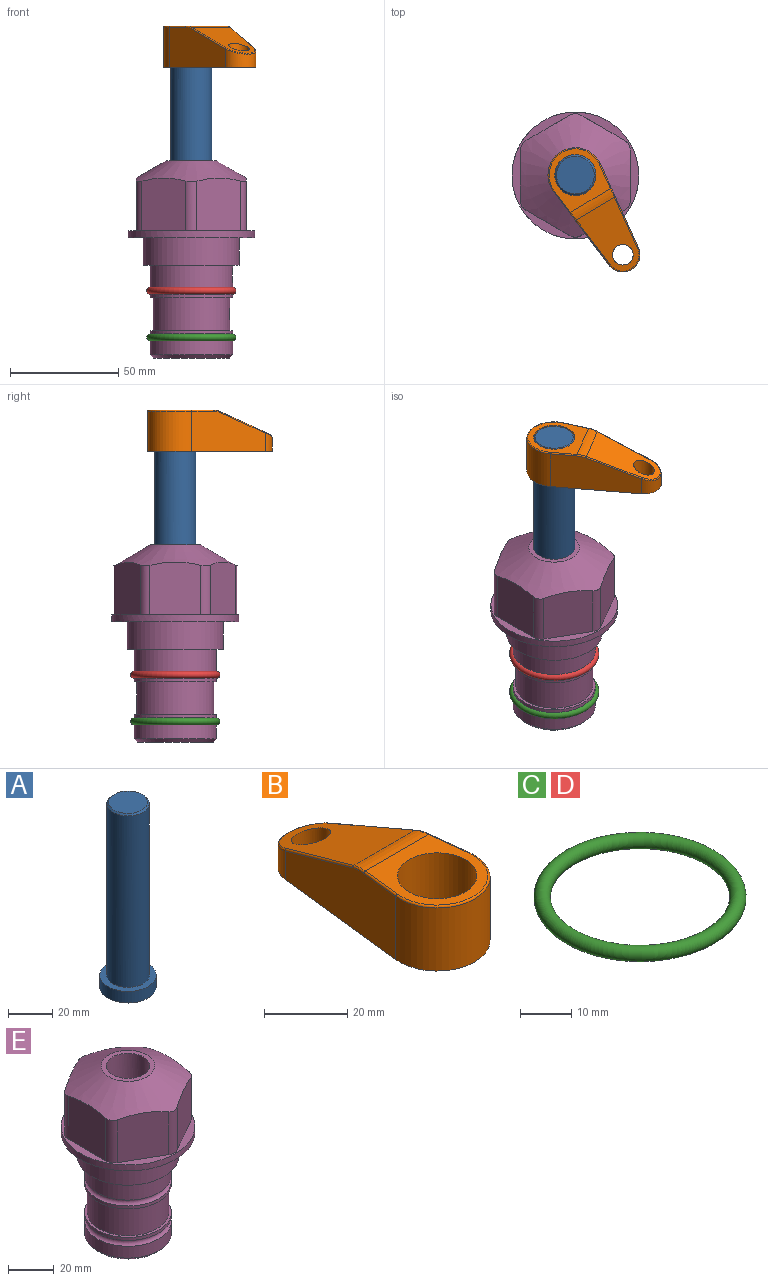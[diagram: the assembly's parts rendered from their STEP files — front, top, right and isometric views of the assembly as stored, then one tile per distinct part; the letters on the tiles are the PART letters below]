
ASSEMBLY  parts=5 mates=3
PART A: 6 faces, bbox 25.4x25.4x101.6 mm
  f0: plane 17.46x17.46mm, normal (0,0,1), area 239.5mm2, adj f5
  f1: plane 25.4x25.4mm, normal (0,0,-1), area 506.7mm2, adj f2
  f2: cylinder r=12.7mm len=25.4mm, axis (0,0,1), area 506.7mm2, adj f1,f3
  f3: plane 25.4x25.4mm, normal (0,0,1), area 221.7mm2, adj f2,f4
  f4: cylinder r=9.53mm len=94.46mm, axis (0,0,1), area 5653mm2, adj f3,f5
  f5: cone r=8.73mm half-angle=45deg, axis (0,0,-1), area 64.4mm2, adj f0,f4
PART B: 44 faces, bbox 27.5x64.5x19.1 mm
  f0: plane 2.3x0.95mm, normal (0,0,-1), area 1mm2, adj f25,f30,f34
  f1: plane 63.5x25.4mm, normal (0,0,-1), area 561.7mm2, adj f2,f3,f4,f5,f6,f7,f19,f20
  f2: cylinder r=12.7mm len=25.4mm, axis (0,0,-1), area 792.2mm2, adj f1,f3,f5,f13
  f3: plane 42.33x18.54mm, normal (0.99,0.11,0), area 647mm2, adj f1,f2,f4,f11,f12,f14
  f4: cylinder r=7.94mm len=15.78mm, axis (0,0,-1), area 158.6mm2, adj f1,f3,f5,f16
  f5: plane 42.33x18.54mm, normal (-0.99,0.11,0), area 647mm2, adj f1,f2,f4,f15,f17,f18
  f6: cylinder r=9.53mm len=19.05mm, axis (0,0,-1), area 1140.1mm2, adj f1,f8
  f7: cylinder r=4.76mm len=10.98mm, axis (0,0,-1), area 276.1mm2, adj f1,f9
  f8: plane 25.83x24.38mm, normal (0,0,1), area 262.2mm2, adj f6,f10,f11,f13,f15
  f9: plane 32.49x20.55mm, normal (0,0.34,0.94), area 489.9mm2, adj f7,f10,f14,f16,f18
  f10: cylinder r=12.7mm len=21.49mm, axis (-1,0,0), area 93.2mm2, adj f8,f9,f12,f17
  f11: cylinder r=0.51mm len=12.34mm, axis (0.11,-0.99,0), area 9.9mm2, adj f3,f8,f12,f13
  f12: bspline ~7.62x1.64mm, area 3.5mm2, adj f3,f10,f11,f14
  f13: torus R=12.19mm, axis (0,0,1), area 33.6mm2, adj f2,f8,f11,f15
  f14: cylinder r=0.51mm len=26.01mm, axis (0.1,-0.93,0.34), area 21.6mm2, adj f3,f9,f12,f16
  f15: cylinder r=0.51mm len=12.34mm, axis (0.11,0.99,0), area 9.9mm2, adj f5,f8,f13,f17
  f16: bspline ~15.78x7.05mm, area 15.7mm2, adj f4,f9,f14,f18
  f17: bspline ~7.62x1.64mm, area 3.5mm2, adj f5,f10,f15,f18
  f18: cylinder r=0.51mm len=26.01mm, axis (0.1,0.93,-0.34), area 21.6mm2, adj f5,f9,f16,f17
  f19: plane 21.6x14.29mm, normal (-0.99,-0.11,0), area 242.6mm2, adj f1,f26,f28,f34,f36,f38
  f20: plane 21.6x14.29mm, normal (0.99,-0.11,0), area 242.6mm2, adj f1,f27,f29,f37,f39,f41
  f21: cylinder r=12.7mm len=14.29mm, axis (0,0,-1), area 173.2mm2, adj f1,f26,f27,f30,f31,f33
  f22: cylinder r=7.94mm len=7.63mm, axis (0,0,-1), area 53.8mm2, adj f1,f28,f29,f42
  f23: plane 2.3x0.95mm, normal (0,0,-1), area 1mm2, adj f25,f33,f37
  f24: plane 17.94x12.32mm, normal (0,-0.34,-0.94), area 191.2mm2, adj f25,f38,f41,f42
  f25: cylinder r=9.53mm len=12.93mm, axis (-1,0,0), area 37.5mm2, adj f0,f23,f24,f31,f36,f39
  f26: cylinder r=1.59mm len=14.29mm, axis (0,0,-1), area 49mm2, adj f1,f19,f21,f32
  f27: cylinder r=1.59mm len=14.29mm, axis (0,0,-1), area 49mm2, adj f1,f20,f21,f35
  f28: cylinder r=1.59mm len=7.28mm, axis (0,0,-1), area 22.1mm2, adj f1,f19,f22,f40
  f29: cylinder r=1.59mm len=7.28mm, axis (0,0,-1), area 22.1mm2, adj f1,f20,f22,f43
  f30: torus R=14.29mm, axis (0,0,1), area 5.8mm2, adj f0,f21,f31,f32
  f31: bspline ~11.06x2.73mm, area 20.8mm2, adj f21,f25,f30,f33
  f32: sphere r=1.59mm, area 5.4mm2, adj f26,f30,f34
  f33: torus R=14.29mm, axis (0,0,1), area 5.8mm2, adj f21,f23,f31,f35
  f34: cylinder r=1.59mm len=1.68mm, axis (-0.11,0.99,0), area 2.4mm2, adj f0,f19,f32,f36
  f35: sphere r=1.59mm, area 5.4mm2, adj f27,f33,f37
  f36: bspline ~5.82x2.33mm, area 7.7mm2, adj f19,f25,f34,f38
  f37: cylinder r=1.59mm len=1.68mm, axis (0.11,0.99,0), area 2.4mm2, adj f20,f23,f35,f39
  f38: cylinder r=1.59mm len=18.33mm, axis (0.1,-0.93,0.34), area 46.7mm2, adj f19,f24,f36,f40
  f39: bspline ~5.82x2.33mm, area 7.7mm2, adj f20,f25,f37,f41
  f40: sphere r=1.59mm, area 3.6mm2, adj f28,f38,f42
  f41: cylinder r=1.59mm len=18.33mm, axis (0.1,0.93,-0.34), area 46.7mm2, adj f20,f24,f39,f43
  f42: bspline ~8.31x1.84mm, area 15.3mm2, adj f22,f24,f40,f43
  f43: sphere r=1.59mm, area 3.6mm2, adj f29,f41,f42
PART C: 1 faces, bbox 44.7x44.7x3.2 mm
  f0: torus R=19.05mm, axis (0,0,1), area 1193.9mm2
PART D: same geometry as C
PART E: 36 faces, bbox 58.7x58.7x91.2 mm
  f0: cylinder r=17.78mm len=35.56mm, axis (0,0,1), area 1670.8mm2, adj f23,f24,f31
  f1: cylinder r=19.05mm len=38.1mm, axis (0,0,1), area 1191.9mm2, adj f26,f27,f30
  f2: plane 58.66x58.66mm, normal (0,0,-1), area 1150.6mm2, adj f3,f28
  f3: cylinder r=29.33mm len=58.66mm, axis (0,0,-1), area 585.1mm2, adj f2,f4
  f4: plane 58.66x58.66mm, normal (0,0,1), area 475.9mm2, adj f3,f5,f6,f7,f8,f9,f10,f11
  f5: plane 24.5x20.32mm, normal (-0.5,0.87,0), area 562.8mm2, adj f4,f15,f16,f17
  f6: plane 24.5x20.32mm, normal (0.5,0.87,0), area 562.8mm2, adj f4,f14,f15,f17
  f7: plane 24.5x23.48mm, normal (1,0,0), area 562.8mm2, adj f4,f13,f14,f17
  f8: plane 24.5x20.32mm, normal (0.5,-0.87,0), area 562.8mm2, adj f4,f12,f13,f17
  f9: plane 24.5x20.32mm, normal (-0.5,-0.87,0), area 562.8mm2, adj f4,f11,f12,f17
  f10: plane 24.5x23.48mm, normal (-1,0,0), area 562.8mm2, adj f4,f11,f16,f17
  f11: cylinder r=5.08mm len=23.01mm, axis (0,0,-1), area 121.2mm2, adj f4,f9,f10,f17
  f12: cylinder r=5.08mm len=23.01mm, axis (0,0,-1), area 121.2mm2, adj f4,f8,f9,f17
  f13: cylinder r=5.08mm len=23.01mm, axis (0,0,-1), area 121.2mm2, adj f4,f7,f8,f17
  f14: cylinder r=5.08mm len=23.01mm, axis (0,0,-1), area 121.2mm2, adj f4,f6,f7,f17
  f15: cylinder r=5.08mm len=23.01mm, axis (0,0,-1), area 121.2mm2, adj f4,f5,f6,f17
  f16: cylinder r=5.08mm len=23.01mm, axis (0,0,-1), area 121.2mm2, adj f4,f5,f10,f17
  f17: cone r=11.73mm half-angle=60deg, axis (0,0,-1), area 2071.8mm2, adj f5,f6,f7,f8,f9,f10,f11,f12
  f18: plane 23.46x23.46mm, normal (0,0,1), area 147.4mm2, adj f17,f35
  f19: plane 34.93x34.93mm, normal (0,0,-1), area 958mm2, adj f29
  f20: cylinder r=19.05mm len=38.1mm, axis (0,0,1), area 760.1mm2, adj f21,f29
  f21: torus R=19.05mm, axis (0,0,1), area 565.3mm2, adj f20,f22
  f22: cylinder r=19.05mm len=38.1mm, axis (0,0,1), area 190mm2, adj f21,f23
  f23: plane 38.1x38.1mm, normal (0,0,1), area 146.9mm2, adj f0,f22
  f24: plane 38.1x38.1mm, normal (0,0,-1), area 146.9mm2, adj f0,f25
  f25: cylinder r=19.05mm len=38.1mm, axis (0,0,1), area 190mm2, adj f24,f26
  f26: torus R=19.05mm, axis (0,0,1), area 565.3mm2, adj f1,f25
  f27: plane 44.45x44.45mm, normal (0,0,-1), area 411.7mm2, adj f1,f28
  f28: cylinder r=22.23mm len=44.45mm, axis (0,0,1), area 1773.5mm2, adj f2,f27
  f29: cone r=19.05mm half-angle=45deg, axis (0,0,1), area 257.5mm2, adj f19,f20
  f30: cylinder r=3.17mm len=6.75mm, axis (-1,0,0), area 128mm2, adj f1,f33
  f31: cylinder r=3.17mm len=6.35mm, axis (-1,0,0), area 102.5mm2, adj f0,f33
  f32: plane 25.4x25.4mm, normal (0,0,1), area 506.7mm2, adj f33
  f33: cylinder r=12.7mm len=66.42mm, axis (0,0,-1), area 5236.2mm2, adj f30,f31,f32,f34
  f34: cone r=9.53mm half-angle=30deg, axis (0,0,-1), area 443.4mm2, adj f33,f35
  f35: cylinder r=9.53mm len=19.05mm, axis (0,0,-1), area 849mm2, adj f18,f34
PLACE A rot(axis=(0,0,-1),59.2deg) t=(0,0,24.35)mm
PLACE B rot(axis=(0,0,-1),149.2deg) t=(0,0,78.96)mm
PLACE C t=(0,0,-21.59)mm
PLACE D at identity
PLACE E at identity fixed
MATE fastened C.f0 <-> E.f0  axis (0,0,1) through (0,0,-46.1)mm
MATE cylindrical A.f2 <-> E.f0  axis (0,0,1) through (0,0,49.99)mm
MATE fastened B.f2 <-> A.f2  axis (0,0,1) through (0,0,98.01)mm
